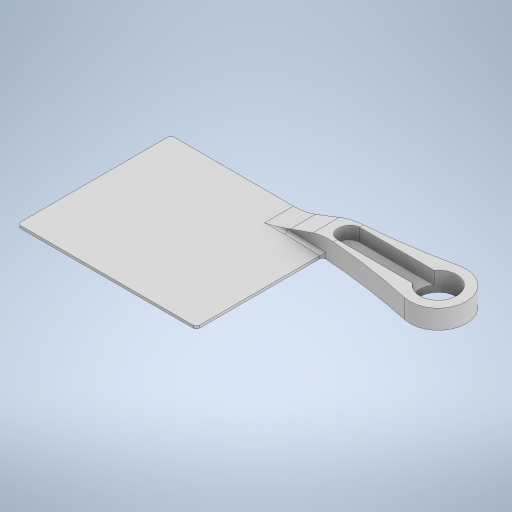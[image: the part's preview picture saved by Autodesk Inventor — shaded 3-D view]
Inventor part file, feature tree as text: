
AUTODESK INVENTOR PART (.ipt)
format: ipt  version: 2023 (Build 270158000, 158)  size: 334,336 bytes
history: native  units: mm
features: extrude x6, sketch x6, fillet x4, projected_geometry x4, other x1, chamfer x1
ambient origin geometry x8: Origin, YZ Plane, XZ Plane, XY Plane, X Axis, Y Axis, Z Axis, Center Point
bodies: Body1 (feature_tree)
feature tree (22):
  other  "Bryła1"
  extrude  "Wyciągnięcie proste1"  Depth=5.8mm
  extrude  "Wyciągnięcie proste2"  Depth=1.5mm
  extrude  "Wyciągnięcie proste3"  Depth=43.875mm
  extrude  "Wyciągnięcie proste4"  Depth=4.0mm
  extrude  "Wyciągnięcie proste5"  Depth=2.0mm TaperAngle=0.0deg
  extrude  "Wyciągnięcie proste6"  Depth=28.0mm
  chamfer  "Faza1"  Distance=20.0mm
  fillet  "Zaokrąglenie4"  Radius=2.0mm
  fillet  "Zaokrąglenie5"  Radius=14.0mm
  fillet  "Zaokrąglenie6"  Radius=3.4mm
  fillet  "Zaokrąglenie7"  Radius=1.0mm
  sketch  "Szkic1"
  sketch  "Szkic2"
  projected_geometry  "Pętla rzutowana1"
  sketch  "Szkic3"
  sketch  "Szkic4"
  projected_geometry  "Pętla rzutowana2"
  sketch  "Szkic5"
  projected_geometry  "Pętla rzutowana3"
  sketch  "Szkic6"
  projected_geometry  "Pętla rzutowana4"
